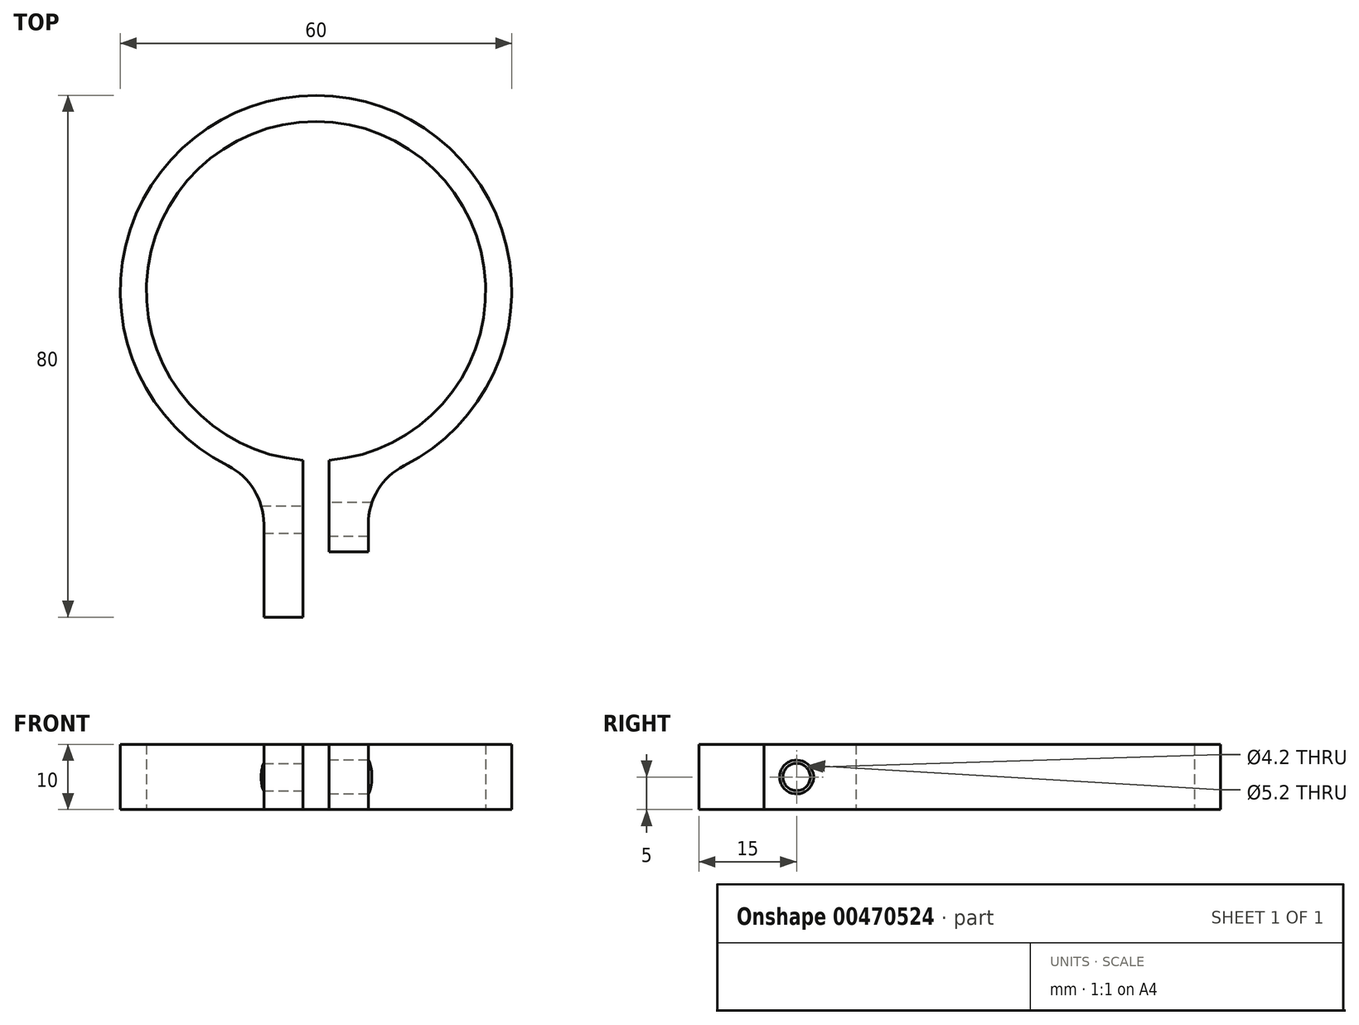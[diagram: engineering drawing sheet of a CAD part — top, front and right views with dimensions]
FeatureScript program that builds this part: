
annotation { "Feature Type Name" : "Feature", "Feature Type Description" : "" }
export const myFeature = defineFeature(function(context is Context, id is Id, definition is map)
    precondition{}
    {
        {
            var Q0;
            Q0=qCreatedBy(makeId("Top.planeOp"),FACE);
            var sketch = newSketch(context, id + "F0", { "sketchPlane" : qUnion([Q0])});
            skArc(sketch, "E0", {"start": v(2, -25.92) * mm, "mid": v(0, 26) * mm, "end": v(-2, -25.92) * mm});
            skArc(sketch, "E1", {"start": v(13.5, -26.8) * mm, "mid": v(0, 30) * mm, "end": v(-13.5, -26.8) * mm});
            skLineSegment(sketch, "E2", {"start": v(8, -35.72) * mm, "end": v(8, -40) * mm});
            skLineSegment(sketch, "E3", {"start": v(-8, -35.72) * mm, "end": v(-8, -50) * mm});
            skLineSegment(sketch, "E4", {"start": v(2, -25.92) * mm, "end": v(2, -40) * mm});
            skLineSegment(sketch, "E5", {"start": v(-2, -25.92) * mm, "end": v(-2, -50) * mm});
            skPoint(sketch, "E6.end.orphan", {"position": v(0, -50) * mm});
            skLineSegment(sketch, "E7", {"start": v(-8, -50) * mm, "end": v(-2, -50) * mm});
            skPoint(sketch, "E8.visualSharp", {"position": v(-8, -28.91) * mm});
            skArc(sketch, "E8.filletArc", {"start": v(-8, -35.72) * mm, "mid": v(-9.49, -30.48) * mm, "end": v(-13.5, -26.8) * mm});
            skPoint(sketch, "E9.visualSharp", {"position": v(8, -28.91) * mm});
            skArc(sketch, "E9.filletArc", {"start": v(13.5, -26.8) * mm, "mid": v(9.49, -30.48) * mm, "end": v(8, -35.72) * mm});
            skLineSegment(sketch, "E10.top", {"start": v(8, -40) * mm, "end": v(2, -40) * mm});
            skPoint(sketch, "E11.trimOffspring.end.orphan", {"position": v(8, -50) * mm});
            skSolve(sketch);
        }
        {
            var Q0;
            Q0 = qSketchRegion(id + "F0", true);
            extrude(context, id + "F1", {"entities" : qUnion([Q0]), "depth" : 10 * mm});
        }
        {
            var Q0;
            Q0=qCreatedBy(makeId("Right.planeOp"),FACE);
            var sketch = newSketch(context, id + "F2", { "sketchPlane" : qUnion([Q0])});
            skLineSegment(sketch, "E12", {"start": v(-56.03, 5) * mm, "end": v(-37.1, 5) * mm});
            skCircle(sketch, "E13", {"center": v(-35, 5) * mm, "radius": 2.1 * mm});
            skLineSegment(sketch, "E14.trimOffspring", {"start": v(-32.9, 5) * mm, "end": v(28.24, 5) * mm});
            skSolve(sketch);
        }
        {
            var Q0;
            Q0 = qSketchRegion(id + "F2", true);
            extrude(context, id + "F3", {"entities" : qUnion([Q0]), "operationType" : NewBodyOperationType.REMOVE, "oppositeDirection" : true, "depth" : 25 * mm});
        }
        {
            var Q0;
            Q0=qCreatedBy(makeId("Right.planeOp"),FACE);
            var sketch = newSketch(context, id + "F4", { "sketchPlane" : qUnion([Q0])});
            skCircle(sketch, "E15", {"center": v(-35, 5) * mm, "radius": 2.6 * mm});
            skSolve(sketch);
        }
        {
            var Q0;
            Q0 = qSketchRegion(id + "F4", true);
            extrude(context, id + "F5", {"entities" : qUnion([Q0]), "operationType" : NewBodyOperationType.REMOVE, "depth" : 25 * mm});
        }
    });
